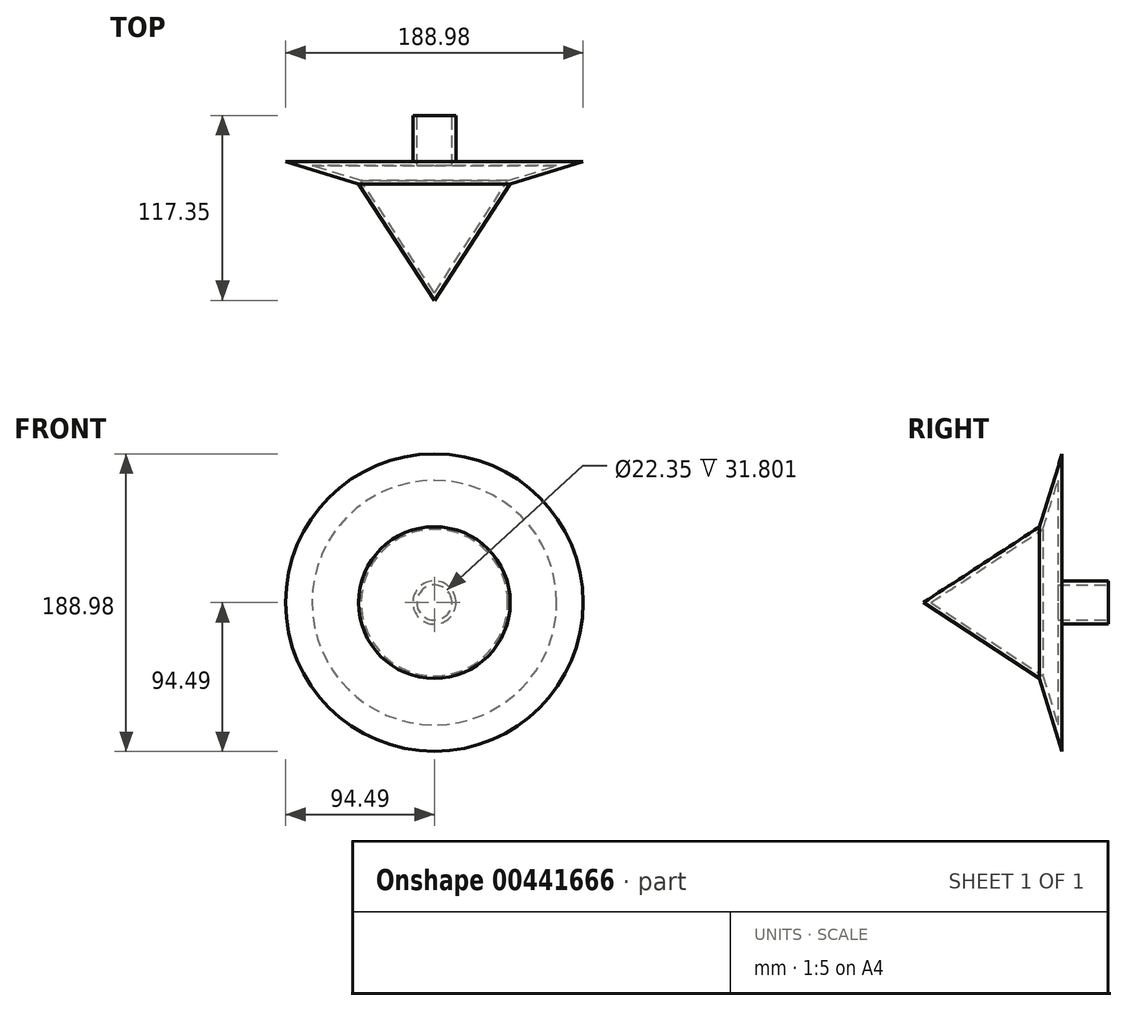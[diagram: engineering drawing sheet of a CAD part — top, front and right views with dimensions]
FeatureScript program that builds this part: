
annotation { "Feature Type Name" : "Feature", "Feature Type Description" : "" }
export const myFeature = defineFeature(function(context is Context, id is Id, definition is map)
    precondition{}
    {
        {
            var Q0;
            Q0=qCreatedBy(makeId("Top.planeOp"),FACE);
            var sketch = newSketch(context, id + "F0", { "sketchPlane" : qUnion([Q0])});
            skPoint(sketch, "E0.start.orphan", {"position": v(0, 61.72) * mm});
            skLineSegment(sketch, "E1", {"start": v(0, 61.72) * mm, "end": v(-13.72, 61.72) * mm});
            skLineSegment(sketch, "E2", {"start": v(-13.72, 61.72) * mm, "end": v(-13.72, 32.46) * mm});
            skLineSegment(sketch, "E3", {"start": v(0, 75.74) * mm, "end": v(0, -55.63) * mm});
            skLineSegment(sketch, "E4", {"start": v(-13.72, 32.46) * mm, "end": v(-29.87, 32.46) * mm});
            skLineSegment(sketch, "E5", {"start": v(-29.87, 32.46) * mm, "end": v(-94.49, 32.46) * mm});
            skLineSegment(sketch, "E6", {"start": v(-94.49, 32.46) * mm, "end": v(-48.16, 18.14) * mm});
            skLineSegment(sketch, "E7", {"start": v(-48.16, 18.14) * mm, "end": v(0, -55.63) * mm});
            skSolve(sketch);
        }
        {
            var Q0;
            Q0 = qSketchRegion(id + "F0", true);
            var Q1;
            Q1=sQuery(id+"F0.wireOp",EDGE,"E3");
            revolve(context, id + "F1", {"entities" : qUnion([Q0]), "axis" : qUnion([Q1]), "revolveType" : RevolveType.FULL});
        }
        {
            var Q0;
            Q0=makeQuery(id+"F1.opRevolve","SWEPT_FACE",FACE,{"disambiguationData":[OSD([sQuery(id+"F0.wireOp",EDGE,"E1")])]});
            shell(context, id + "F2", {"entities" : qUnion([Q0]), "thickness" : 2.54 * mm});
        }
    });
